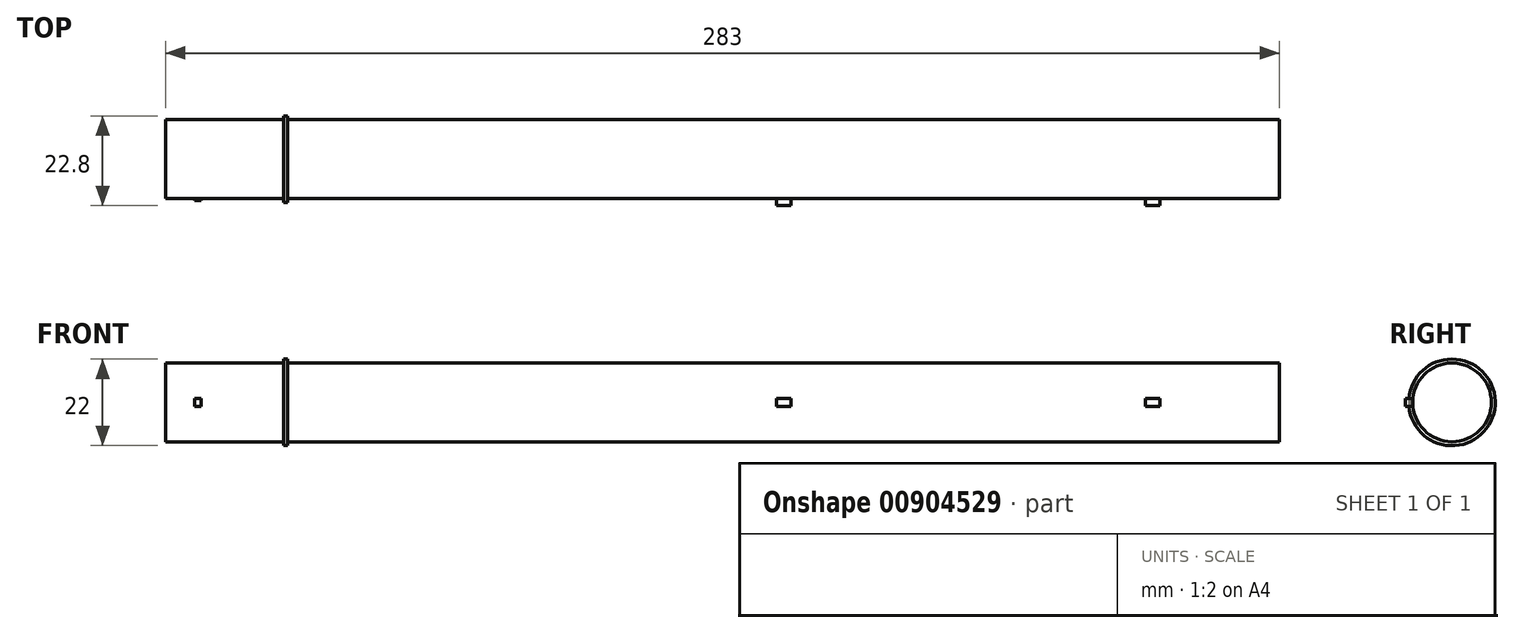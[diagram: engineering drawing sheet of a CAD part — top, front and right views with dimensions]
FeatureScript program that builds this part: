
annotation { "Feature Type Name" : "Feature", "Feature Type Description" : "" }
export const myFeature = defineFeature(function(context is Context, id is Id, definition is map)
    precondition{}
    {
        {
            var Q0;
            Q0=qCreatedBy(makeId("Front.planeOp"),FACE);
            var sketch = newSketch(context, id + "F0", { "sketchPlane" : qUnion([Q0])});
            skLineSegment(sketch, "E0", {"start": v(-34.16, 10) * mm, "end": v(67.84, 10) * mm});
            skLineSegment(sketch, "E1", {"start": v(102, 0) * mm, "end": v(0, 0) * mm});
            skLineSegment(sketch, "E2", {"start": v(-34.16, 10) * mm, "end": v(-34.16, 11) * mm});
            skLineSegment(sketch, "E3", {"start": v(-34.16, 11) * mm, "end": v(-35.16, 11) * mm});
            skLineSegment(sketch, "E4", {"start": v(-35.16, 11) * mm, "end": v(-35.16, 10) * mm});
            skLineSegment(sketch, "E5", {"start": v(-35.16, 10) * mm, "end": v(-65.16, 10) * mm});
            skLineSegment(sketch, "E6", {"start": v(-65.16, 10) * mm, "end": v(-65.16, 0) * mm});
            skLineSegment(sketch, "E7", {"start": v(-65.16, 0) * mm, "end": v(0, 0) * mm});
            skLineSegment(sketch, "E8", {"start": v(67.84, 10) * mm, "end": v(86.3, 10) * mm});
            skLineSegment(sketch, "E9", {"start": v(217.84, 10) * mm, "end": v(217.84, 0) * mm});
            skLineSegment(sketch, "E10", {"start": v(217.84, 0) * mm, "end": v(102, 0) * mm});
            skLineSegment(sketch, "E11.trimOffspring", {"start": v(86.3, 10) * mm, "end": v(176.3, 10) * mm});
            skLineSegment(sketch, "E12.trimOffspring", {"start": v(176.3, 10) * mm, "end": v(217.84, 10) * mm});
            skSolve(sketch);
        }
        {
            var Q0;
            Q0=makeQuery(id+"F0.imprint","IMPRINT",FACE,{"disambiguationData":[TD([[makeQuery(id+"F0.imprint","IMPRINT",EDGE,{"derivedFrom":sQuery(id+"F0.wireOp",EDGE,"E0")}),-1.0]])]});
            var Q1;
            Q1=sQuery(id+"F0.wireOp",EDGE,"E7");
            revolve(context, id + "F1", {"surfaceOperationType" : NewSurfaceOperationType.NEW, "entities" : qUnion([Q0]), "axis" : qUnion([Q1]), "revolveType" : RevolveType.FULL});
        }
        {
            var Q0;
            Q0=qCreatedBy(makeId("Top.planeOp"),FACE);
            var sketch = newSketch(context, id + "F2", { "sketchPlane" : qUnion([Q0])});
            skLineSegment(sketch, "E13.bottom", {"start": v(-57.85, -10.5) * mm, "end": v(-56.16, -10.5) * mm});
            skLineSegment(sketch, "E13.top", {"start": v(-57.85, -10) * mm, "end": v(-56.16, -10) * mm});
            skLineSegment(sketch, "E13.left", {"start": v(-57.85, -10.5) * mm, "end": v(-57.85, -10) * mm});
            skLineSegment(sketch, "E13.right", {"start": v(-56.16, -10.5) * mm, "end": v(-56.16, -10) * mm});
            skLineSegment(sketch, "E14.bottom", {"start": v(90, -11.8) * mm, "end": v(93.7, -11.8) * mm});
            skLineSegment(sketch, "E14.top", {"start": v(90, -10) * mm, "end": v(93.7, -10) * mm});
            skLineSegment(sketch, "E14.left", {"start": v(90, -11.8) * mm, "end": v(90, -10) * mm});
            skLineSegment(sketch, "E14.right", {"start": v(93.7, -11.8) * mm, "end": v(93.7, -10) * mm});
            skLineSegment(sketch, "E15.bottom", {"start": v(183.7, -11.8) * mm, "end": v(187.4, -11.8) * mm});
            skLineSegment(sketch, "E15.top", {"start": v(183.7, -10) * mm, "end": v(187.4, -10) * mm});
            skLineSegment(sketch, "E15.left", {"start": v(183.7, -11.8) * mm, "end": v(183.7, -10) * mm});
            skLineSegment(sketch, "E15.right", {"start": v(187.4, -11.8) * mm, "end": v(187.4, -10) * mm});
            skSolve(sketch);
        }
        {
            var Q0;
            Q0=qSketchRegion(id+"F2",true);
            extrude(context, id + "F3", {"entities" : qUnion([Q0]), "operationType" : NewBodyOperationType.ADD, "depth" : 2 * mm, "offsetDistance" : 25 * mm, "symmetric" : true});
        }
    });
